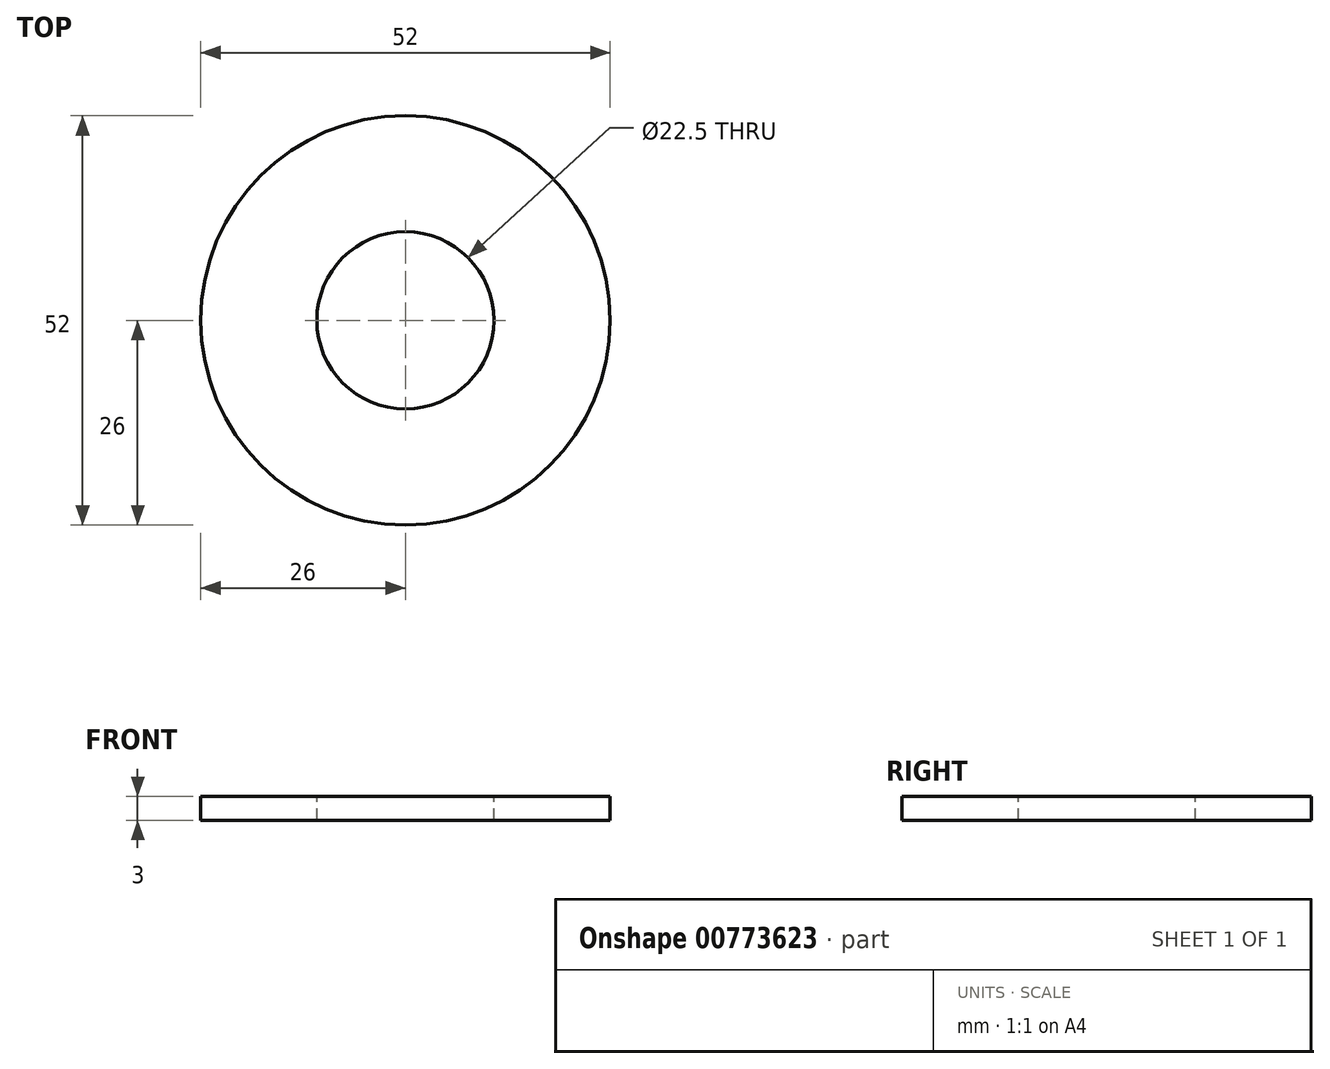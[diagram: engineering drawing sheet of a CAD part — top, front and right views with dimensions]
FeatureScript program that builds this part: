
annotation { "Feature Type Name" : "Feature", "Feature Type Description" : "" }
export const myFeature = defineFeature(function(context is Context, id is Id, definition is map)
    precondition{}
    {
        {
            var Q0;
            Q0=qCreatedBy(makeId("Top.planeOp"),FACE);
            var sketch = newSketch(context, id + "F0", { "sketchPlane" : qUnion([Q0])});
            skCircle(sketch, "E0", {"center": v(0, 0) * mm, "radius": 11.25 * mm});
            skCircle(sketch, "E1", {"center": v(0, 0) * mm, "radius": 26 * mm});
            skSolve(sketch);
        }
        {
            var Q0;
            Q0=makeQuery(id+"F0.imprint","IMPRINT",FACE,{"disambiguationData":[TD([[makeQuery(id+"F0.imprint","IMPRINT",EDGE,{"derivedFrom":sQuery(id+"F0.wireOp",EDGE,"8VPymfjl-yQQ9-dhi0-yzJW-p6myARYrwqGD")}),-1.0]])]});
            var Q1;
            Q1=makeQuery(id+"F0.imprint","IMPRINT",FACE,{"disambiguationData":[TD([[makeQuery(id+"F0.imprint","IMPRINT",EDGE,{"derivedFrom":sQuery(id+"F0.wireOp",EDGE,"E0")}),-1.0]])]});
            extrude(context, id + "F1", {"entities" : qUnion([Q0, Q1]), "oppositeDirection" : true, "depth" : 3 * mm, "offsetDistance" : 25 * mm});
        }
    });
